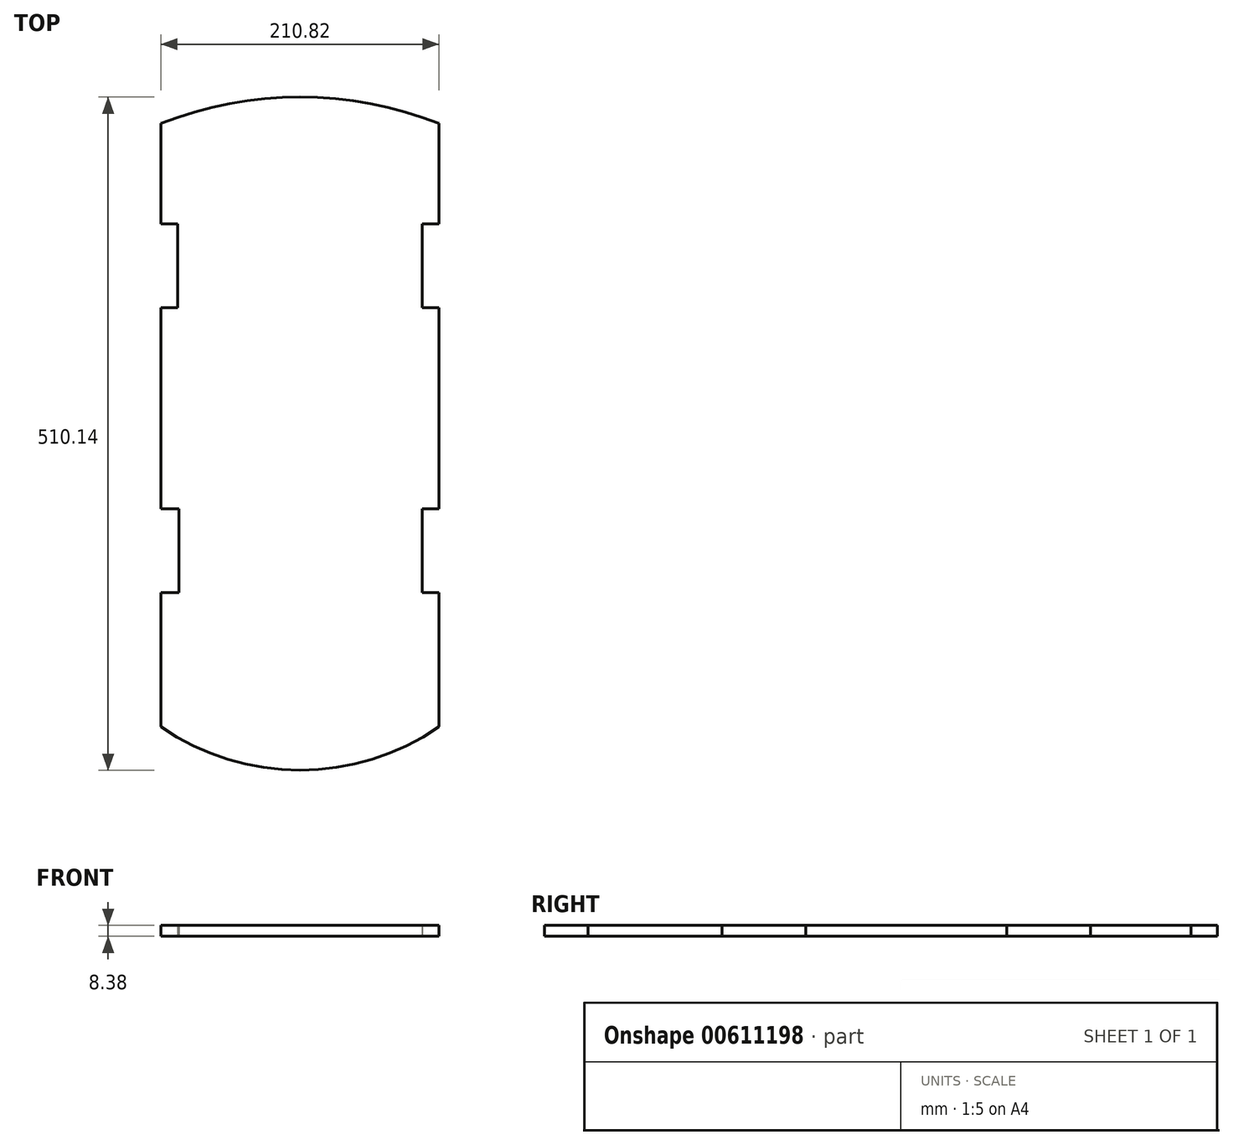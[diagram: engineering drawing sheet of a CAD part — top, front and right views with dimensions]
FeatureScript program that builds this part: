
annotation { "Feature Type Name" : "Feature", "Feature Type Description" : "" }
export const myFeature = defineFeature(function(context is Context, id is Id, definition is map)
    precondition{}
    {
        {
            var Q0;
            Q0=qCreatedBy(makeId("Top.planeOp"),FACE);
            var sketch = newSketch(context, id + "F0", { "sketchPlane" : qUnion([Q0])});
            skLineSegment(sketch, "E0", {"start": v(-70, 225.65) * mm, "end": v(-70, 149.45) * mm});
            skLineSegment(sketch, "E1", {"start": v(-70, 149.45) * mm, "end": v(-57.3, 149.45) * mm});
            skLineSegment(sketch, "E2", {"start": v(-57.3, 149.45) * mm, "end": v(-57.3, 85.95) * mm});
            skLineSegment(sketch, "E3", {"start": v(-57.3, 85.95) * mm, "end": v(-70, 85.95) * mm});
            skLineSegment(sketch, "E4", {"start": v(-70, 85.95) * mm, "end": v(-70, -66.45) * mm});
            skLineSegment(sketch, "E5", {"start": v(-70, -66.45) * mm, "end": v(-56.3, -66.45) * mm});
            skLineSegment(sketch, "E6", {"start": v(-56.3, -66.45) * mm, "end": v(-56.3, -129.95) * mm});
            skLineSegment(sketch, "E7", {"start": v(-56.3, -129.95) * mm, "end": v(-70, -129.95) * mm});
            skLineSegment(sketch, "E8", {"start": v(-70, -129.95) * mm, "end": v(-70, -231.55) * mm});
            skArc(sketch, "E9", {"start": v(-70, -231.55) * mm, "mid": v(35.42, -264.43) * mm, "end": v(140.83, -231.55) * mm});
            skLineSegment(sketch, "E10", {"start": v(140.83, -231.55) * mm, "end": v(140.83, -129.95) * mm});
            skLineSegment(sketch, "E11", {"start": v(140.83, -129.95) * mm, "end": v(128.13, -129.95) * mm});
            skLineSegment(sketch, "E12", {"start": v(128.13, -129.95) * mm, "end": v(128.13, -66.45) * mm});
            skLineSegment(sketch, "E13", {"start": v(128.13, -66.45) * mm, "end": v(140.83, -66.45) * mm});
            skLineSegment(sketch, "E14", {"start": v(140.83, -66.45) * mm, "end": v(140.83, 85.95) * mm});
            skLineSegment(sketch, "E15", {"start": v(140.83, 85.95) * mm, "end": v(128.13, 85.95) * mm});
            skLineSegment(sketch, "E16", {"start": v(128.13, 85.95) * mm, "end": v(128.13, 149.45) * mm});
            skLineSegment(sketch, "E17", {"start": v(128.13, 149.45) * mm, "end": v(140.83, 149.45) * mm});
            skLineSegment(sketch, "E18", {"start": v(140.83, 149.45) * mm, "end": v(140.83, 225.65) * mm});
            skArc(sketch, "E19", {"start": v(140.83, 225.65) * mm, "mid": v(35.42, 245.7) * mm, "end": v(-70, 225.65) * mm});
            skSolve(sketch);
        }
        {
            var Q0;
            Q0 = qSketchRegion(id + "F0", true);
            extrude(context, id + "F1", {"entities" : qUnion([Q0]), "depth" : 8.38 * mm, "offsetDistance" : 25.4 * mm});
        }
    });
